# Revit family: STH20992BR_27_40_STH20992PTO_27
name_source: partatom
category: Luminárias
units: mm (PartAtom-declared; Revit-internal decimal feet)

## family parameters
Compartilhado = Não
Corte com vazios quando carregada = Não
Cota do conector redondo = Utilizar diâmetro
Fonte luminosa = Não
Hospedeiro = Forro
Manter orientação da anotação = Não
Número OmniClass = 23.80.70.11
Ponto de cálculo do ambiente = Não
Sempre na vertical = Sim
Tipo de parte = Normal
Título OmniClass = Luminaries for Internal Lighting

## types (3) — shared parameters
Altura = 0.04 m
Comprimento = 2.02 m
Dimerização = Não dimerizável
Fabricante = Stella
Grau de proteção (IP) = IP20
IRC (Índice de reprodução de cores) = >93 (R9 >60)
Largura = 0.05 m
Modelo = Archi
Tensão Elétrica = 24V
URL = https://stella.com.br
Ângulo de Abertura = 100°
zero-valued in all types: Elevação padrão

## per-type parameters (varying)
| type | Estrutura | Fluxo Luminoso | Fluxo Luminoso STH20992BR/27 | Fluxo Luminoso STH20992BR/40 | Fluxo Luminoso STH20992PTO/27 | Luminoso | Potência | Referência | Temperatura da cor (K) |
| STH20992BR/27 - BRANCO - 2m - 2700K - 2000lm - 100° | Al - Branco | 2000 lm | Sim | Não | Não | Luminoso - 2700K | 46 W | STH20992BR/27 - BRANCO - 2m | 2700 K |
| STH20992BR/40 - BRANCO - 2m - 4000K - 2000lm - 100° | Al - Branco | 2000 lm | Não | Sim | Não | Luminoso - 4000K | 46 W | STH20992BR/40 - BRANCO - 2m | 4000 K |
| STH20992PTO/27 - PRETO - 2m - 2700K - 1500lm - 90° | Al - Preto | 1500 lm | Não | Não | Sim | Luminoso - 2700K | 56 W | STH20992PTO/27 - PRETO - 2m | 2700 K |
